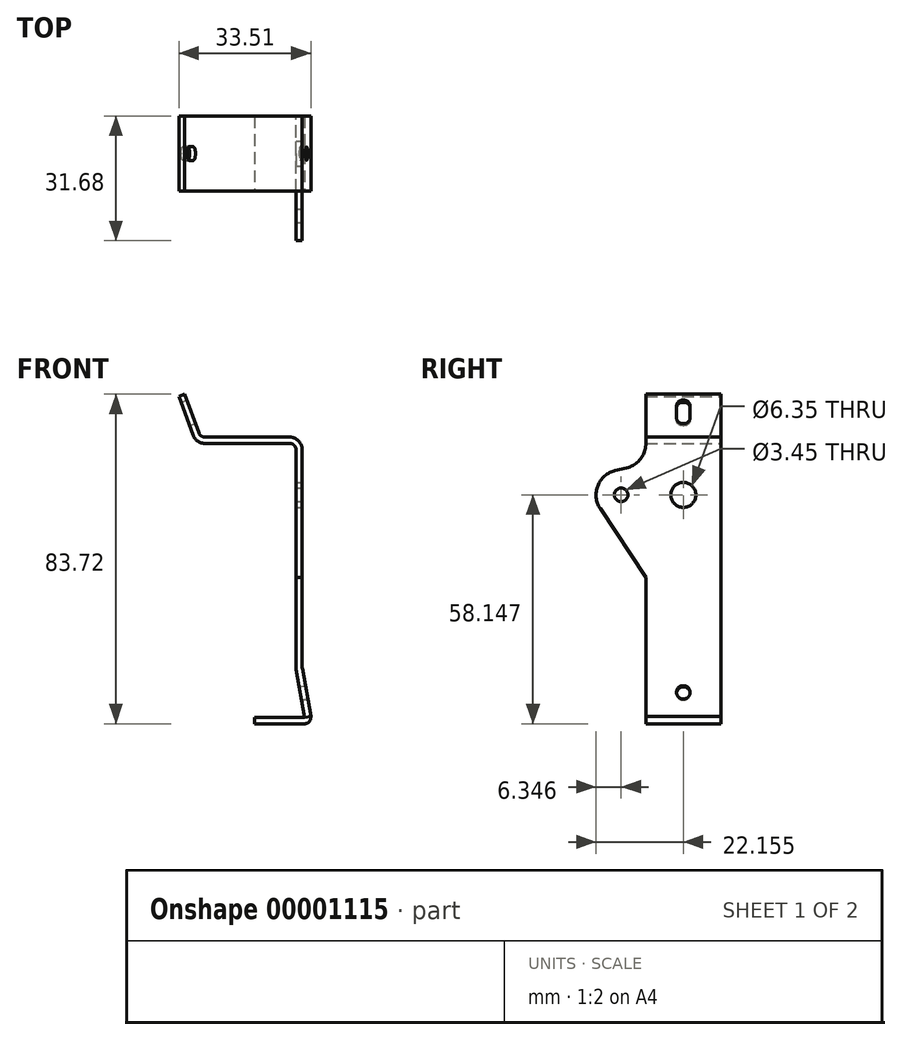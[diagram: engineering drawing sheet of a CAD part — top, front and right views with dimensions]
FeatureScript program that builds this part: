
annotation { "Feature Type Name" : "Feature", "Feature Type Description" : "" }
export const myFeature = defineFeature(function(context is Context, id is Id, definition is map)
    precondition{}
    {
        {
            var Q0;
            Q0=qCreatedBy(makeId("Front.planeOp"),FACE);
            var sketch = newSketch(context, id + "F0", { "sketchPlane" : qUnion([Q0])});
            skLineSegment(sketch, "E0", {"start": v(0, 0.28) * mm, "end": v(0, 55.56) * mm});
            skLineSegment(sketch, "E1", {"start": v(-1.59, 57.15) * mm, "end": v(-23.18, 57.15) * mm});
            skLineSegment(sketch, "E2", {"start": v(-26.16, 59.24) * mm, "end": v(-29.74, 69.08) * mm});
            skLineSegment(sketch, "E3", {"start": v(0.05, -0.27) * mm, "end": v(2.2, -12.5) * mm});
            skLineSegment(sketch, "E4.0", {"start": v(-24.67, 59.78) * mm, "end": v(-28.25, 69.63) * mm});
            skLineSegment(sketch, "E4.1", {"start": v(-1.59, 58.74) * mm, "end": v(-23.18, 58.74) * mm});
            skLineSegment(sketch, "E4.2", {"start": v(1.59, 0.28) * mm, "end": v(1.59, 55.56) * mm});
            skLineSegment(sketch, "E4.3", {"start": v(1.61, 0) * mm, "end": v(3.77, -12.23) * mm});
            skLineSegment(sketch, "E5", {"start": v(-29.74, 69.08) * mm, "end": v(-28.25, 69.63) * mm});
            skLineSegment(sketch, "E6", {"start": v(3.77, -12.23) * mm, "end": v(2.2, -12.5) * mm});
            skPoint(sketch, "E7.visualSharp", {"position": v(1.59, 58.74) * mm});
            skArc(sketch, "E7.filletArc", {"start": v(1.59, 55.56) * mm, "mid": v(0.66, 57.8) * mm, "end": v(-1.59, 58.74) * mm});
            skPoint(sketch, "E8.visualSharp", {"position": v(-25.4, 57.15) * mm});
            skArc(sketch, "E8.filletArc", {"start": v(-26.16, 59.24) * mm, "mid": v(-25, 57.72) * mm, "end": v(-23.18, 57.15) * mm});
            skPoint(sketch, "E9.visualSharp", {"position": v(0, 0) * mm});
            skArc(sketch, "E9.filletArc", {"start": v(0, 0.28) * mm, "mid": v(0.01, 0) * mm, "end": v(0.05, -0.27) * mm});
            skPoint(sketch, "E10.visualSharp", {"position": v(0, 57.15) * mm});
            skArc(sketch, "E10.filletArc", {"start": v(0, 55.56) * mm, "mid": v(-0.46, 56.69) * mm, "end": v(-1.59, 57.15) * mm});
            skPoint(sketch, "E11.visualSharp", {"position": v(-24.29, 58.74) * mm});
            skArc(sketch, "E11.filletArc", {"start": v(-24.67, 59.78) * mm, "mid": v(-24.09, 59.02) * mm, "end": v(-23.18, 58.74) * mm});
            skPoint(sketch, "E12.visualSharp", {"position": v(1.59, 0.14) * mm});
            skArc(sketch, "E12.filletArc", {"start": v(1.59, 0.28) * mm, "mid": v(1.6, 0.14) * mm, "end": v(1.61, 0) * mm});
            skPoint(sketch, "E13", {"position": v(-26.46, 64.7) * mm});
            skPoint(sketch, "E14", {"position": v(-27.95, 64.16) * mm});
            skPoint(sketch, "E15", {"position": v(2.7, -6.11) * mm});
            skPoint(sketch, "E16", {"position": v(1.13, -6.4) * mm});
            skSolve(sketch);
        }
        {
            var Q0;
            Q0=makeQuery(id+"F0.imprint","IMPRINT",FACE,{"disambiguationData":[TD([[makeQuery(id+"F0.imprint","IMPRINT",EDGE,{"derivedFrom":sQuery(id+"F0.wireOp",EDGE,"E0")}),-1.0]])]});
            extrude(context, id + "F1", {"entities" : qUnion([Q0]), "depth" : 19.05 * mm});
        }
        {
            var Q0;
            Q0=makeQuery(id+"F1.opExtrude","SWEPT_FACE",FACE,{"disambiguationData":[OSD([sQuery(id+"F0.wireOp",EDGE,"E4.0")])]});
            var sketch = newSketch(context, id + "F2", { "sketchPlane" : qUnion([Q0])});
            skLineSegment(sketch, "E17.right", {"start": v(0, 75.1) * mm, "end": v(0, 69.85) * mm});
            skLineSegment(sketch, "E18", {"start": v(-11.25, 68.74) * mm, "end": v(-11.25, 71.92) * mm});
            skLineSegment(sketch, "E19", {"start": v(-7.8, 71.92) * mm, "end": v(-7.8, 68.74) * mm});
            skLineSegment(sketch, "E20", {"start": v(-9.66, 73.5) * mm, "end": v(-9.39, 73.5) * mm});
            skLineSegment(sketch, "E21", {"start": v(-9.39, 67.15) * mm, "end": v(-9.66, 67.15) * mm});
            skPoint(sketch, "E22.visualSharp", {"position": v(-11.25, 73.5) * mm});
            skArc(sketch, "E22.filletArc", {"start": v(-9.66, 73.5) * mm, "mid": v(-10.79, 73.04) * mm, "end": v(-11.25, 71.92) * mm});
            skPoint(sketch, "E23.visualSharp", {"position": v(-7.8, 73.5) * mm});
            skArc(sketch, "E23.filletArc", {"start": v(-7.8, 71.92) * mm, "mid": v(-8.26, 73.04) * mm, "end": v(-9.39, 73.5) * mm});
            skPoint(sketch, "E24.visualSharp", {"position": v(-7.8, 67.15) * mm});
            skArc(sketch, "E24.filletArc", {"start": v(-9.39, 67.15) * mm, "mid": v(-8.26, 67.62) * mm, "end": v(-7.8, 68.74) * mm});
            skPoint(sketch, "E25.visualSharp", {"position": v(-11.25, 67.15) * mm});
            skArc(sketch, "E25.filletArc", {"start": v(-11.25, 68.74) * mm, "mid": v(-10.79, 67.62) * mm, "end": v(-9.66, 67.15) * mm});
            skSolve(sketch);
        }
        {
            var Q0;
            Q0=makeQuery(id+"F2.imprint","IMPRINT",FACE,{"disambiguationData":[TD([[makeQuery(id+"F2.imprint","IMPRINT",EDGE,{"derivedFrom":sQuery(id+"F2.wireOp",EDGE,"E18")}),-1.0]])]});
            extrude(context, id + "F3", {"entities" : qUnion([Q0]), "operationType" : NewBodyOperationType.REMOVE, "oppositeDirection" : true, "depth" : 25.4 * mm});
        }
        {
            var Q0;
            Q0=makeQuery(id+"F1.opExtrude","SWEPT_FACE",FACE,{"disambiguationData":[OSD([sQuery(id+"F0.wireOp",EDGE,"E4.3")])]});
            var sketch = newSketch(context, id + "F4", { "sketchPlane" : qUnion([Q0])});
            skCircle(sketch, "E26", {"center": v(-9.53, -6.49) * mm, "radius": 1.73 * mm});
            skSolve(sketch);
        }
        {
            var Q0;
            Q0=makeQuery(id+"F4.imprint","IMPRINT",FACE,{"disambiguationData":[TD([[makeQuery(id+"F4.imprint","IMPRINT",EDGE,{"derivedFrom":sQuery(id+"F4.wireOp",EDGE,"E26")}),1.0]])]});
            extrude(context, id + "F5", {"entities" : qUnion([Q0]), "operationType" : NewBodyOperationType.REMOVE, "oppositeDirection" : true, "depth" : 25.4 * mm});
        }
        {
            var Q0;
            Q0=makeQuery(id+"F1.opExtrude","SWEPT_FACE",FACE,{"disambiguationData":[OSD([sQuery(id+"F0.wireOp",EDGE,"E4.2")])]});
            var sketch = newSketch(context, id + "F6", { "sketchPlane" : qUnion([Q0])});
            skLineSegment(sketch, "E27", {"start": v(-19.05, 55.56) * mm, "end": v(-19.05, 52.1) * mm});
            skLineSegment(sketch, "E28", {"start": v(-19.05, 52.1) * mm, "end": v(-26.82, 50.23) * mm});
            skLineSegment(sketch, "E29", {"start": v(-30.63, 40.55) * mm, "end": v(-19.05, 23.05) * mm});
            skPoint(sketch, "E30.visualSharp", {"position": v(-35.63, 48.11) * mm});
            skArc(sketch, "E30.filletArc", {"start": v(-26.82, 50.23) * mm, "mid": v(-31.24, 46.38) * mm, "end": v(-30.63, 40.55) * mm});
            skPoint(sketch, "E31.0.MirrorP", {"position": v(16.58, 48.11) * mm});
            skArc(sketch, "E31.1.MirrorCS", {"start": v(7.77, 50.23) * mm, "mid": v(12.2, 46.38) * mm, "end": v(11.58, 40.55) * mm});
            skLineSegment(sketch, "E31.2.MirrorCS", {"start": v(11.58, 40.55) * mm, "end": v(0, 23.05) * mm});
            skLineSegment(sketch, "E31.3.MirrorCS", {"start": v(0, 52.1) * mm, "end": v(7.77, 50.23) * mm});
            skSolve(sketch);
        }
        {
            var Q0;
            {var subQ2=sQuery(id+"F6.wireOp",EDGE,"E28");Q0=makeQuery(id+"F6.imprint","IMPRINT",FACE,{"disambiguationData":[TD([[makeQuery(id+"F6.imprint","IMPRINT",EDGE,{"derivedFrom":subQ2}),1.0]])]});}
            var Q1;
            Q1=makeQuery(id+"F6.imprint","IMPRINT",FACE,{"disambiguationData":[TD([[makeQuery(id+"F6.imprint","IMPRINT",EDGE,{"derivedFrom":sQuery(id+"F6.wireOp",EDGE,"E31.1.MirrorCS")}),-1.0]])]});
            extrude(context, id + "F7", {"entities" : qUnion([Q0, Q1]), "operationType" : NewBodyOperationType.ADD, "oppositeDirection" : true, "depth" : 1.59 * mm});
        }
        {
            var Q0;
            {var subQ0=sQuery(id+"F0.wireOp",EDGE,"E4.2");Q0=makeQuery(id+"F7.boolean.opBoolean","MERGE",FACE,{"derivedFrom":[makeQuery(id+"F1.opExtrude","SWEPT_FACE",FACE,{"disambiguationData":[OSD([subQ0])]}),makeQuery(id+"F7.opExtrude","CAP_FACE",FACE,{"disambiguationData":[OSD([subQ0,sQuery(id+"F6.wireOp",EDGE,"E28"),sQuery(id+"F6.wireOp",EDGE,"E29"),sQuery(id+"F6.wireOp",EDGE,"E30.filletArc")])],"isStart":true}),makeQuery(id+"F7.opExtrude","CAP_FACE",FACE,{"disambiguationData":[OSD([subQ0,sQuery(id+"F6.wireOp",EDGE,"E31.1.MirrorCS"),sQuery(id+"F6.wireOp",EDGE,"E31.2.MirrorCS"),sQuery(id+"F6.wireOp",EDGE,"E31.3.MirrorCS")])],"isStart":true})]});}
            var sketch = newSketch(context, id + "F8", { "sketchPlane" : qUnion([Q0])});
            skCircle(sketch, "E32", {"center": v(-25.33, 44.06) * mm, "radius": 1.73 * mm});
            skCircle(sketch, "E33", {"center": v(6.28, 44.06) * mm, "radius": 1.73 * mm});
            skCircle(sketch, "E34", {"center": v(-9.53, 44.06) * mm, "radius": 3.18 * mm});
            skSolve(sketch);
        }
        {
            var Q0;
            {Q0=qUnion([makeQuery(id+"F8.imprint","IMPRINT",FACE,{"disambiguationData":[TD([[makeQuery(id+"F8.imprint","IMPRINT",EDGE,{"derivedFrom":sQuery(id+"F8.wireOp",EDGE,"E32")}),1.0]])]}),makeQuery(id+"F8.imprint","IMPRINT",FACE,{"disambiguationData":[TD([[makeQuery(id+"F8.imprint","IMPRINT",EDGE,{"derivedFrom":sQuery(id+"F8.wireOp",EDGE,"E33")}),1.0]])]}),makeQuery(id+"F8.imprint","IMPRINT",FACE,{"disambiguationData":[TD([[makeQuery(id+"F8.imprint","IMPRINT",EDGE,{"derivedFrom":sQuery(id+"F8.wireOp",EDGE,"E34")}),1.0]])]})]);}
            extrude(context, id + "F9", {"entities" : qUnion([Q0]), "operationType" : NewBodyOperationType.REMOVE, "oppositeDirection" : true, "depth" : 25.4 * mm});
        }
        {
            var Q0;
            Q0=makeQuery(id+"F7.opExtrude","SWEPT_EDGE",EDGE,{"disambiguationData":[OSD([sQuery(id+"F0.wireOp",EDGE,"E4.2"),sQuery(id+"F6.wireOp",EDGE,"E27"),sQuery(id+"F6.wireOp",EDGE,"E28")])]});
            var Q1;
            Q1=makeQuery(id+"F7.opExtrude","SWEPT_EDGE",EDGE,{"disambiguationData":[OSD([sQuery(id+"F0.wireOp",EDGE,"E4.2"),sQuery(id+"F6.wireOp",EDGE,"E31.3.MirrorCS")])]});
            var Q2;
            Q2=makeQuery(id+"F7.opExtrude","SWEPT_EDGE",EDGE,{"disambiguationData":[OSD([sQuery(id+"F0.wireOp",EDGE,"E4.2"),sQuery(id+"F6.wireOp",EDGE,"E31.2.MirrorCS")])]});
            var Q3;
            Q3=makeQuery(id+"F7.opExtrude","SWEPT_EDGE",EDGE,{"disambiguationData":[OSD([sQuery(id+"F0.wireOp",EDGE,"E4.2"),sQuery(id+"F6.wireOp",EDGE,"E29")])]});
            fillet(context, id + "F10", {"entities" : qUnion([Q0, Q1, Q2, Q3]), "radius" : 6.35 * mm, "tangentPropagation" : true, "allowEdgeOverflow" : false});
        }
        {
            var Q0;
            {var subQ0=sQuery(id+"F0.wireOp",EDGE,"E0");var subQ1=sQuery(id+"F0.wireOp",EDGE,"E3");var subQ2=sQuery(id+"F0.wireOp",EDGE,"E4.2");var subQ3=sQuery(id+"F0.wireOp",EDGE,"E4.3");var subQ4=sQuery(id+"F0.wireOp",EDGE,"E6");var subQ5=sQuery(id+"F0.wireOp",EDGE,"E9.filletArc");var subQ6=sQuery(id+"F0.wireOp",EDGE,"E12.filletArc");Q0=makeQuery(id+"F7.boolean.opBoolean","SPLIT",FACE,{"disambiguationData":[TD([makeQuery(id+"F1.opExtrude","SWEPT_FACE",FACE,{"disambiguationData":[OSD([subQ1])]})])],"derivedFrom":makeQuery(id+"F1.opExtrude","CAP_FACE",FACE,{"disambiguationData":[OSD([subQ0,sQuery(id+"F0.wireOp",EDGE,"E1"),sQuery(id+"F0.wireOp",EDGE,"E2"),subQ1,sQuery(id+"F0.wireOp",EDGE,"E4.0"),sQuery(id+"F0.wireOp",EDGE,"E4.1"),subQ2,subQ3,sQuery(id+"F0.wireOp",EDGE,"E5"),subQ4,sQuery(id+"F0.wireOp",EDGE,"E7.filletArc"),sQuery(id+"F0.wireOp",EDGE,"E8.filletArc"),subQ5,sQuery(id+"F0.wireOp",EDGE,"E10.filletArc"),sQuery(id+"F0.wireOp",EDGE,"E11.filletArc"),subQ6])],"isStart":false})});}
            var sketch = newSketch(context, id + "F11", { "sketchPlane" : qUnion([Q0])});
            skLineSegment(sketch, "E35", {"start": v(2.2, -12.5) * mm, "end": v(-10.5, -12.5) * mm});
            skLineSegment(sketch, "E36", {"start": v(-10.5, -12.5) * mm, "end": v(-10.5, -14.1) * mm});
            skLineSegment(sketch, "E37", {"start": v(-10.5, -14.1) * mm, "end": v(3.77, -14.1) * mm});
            skLineSegment(sketch, "E38", {"start": v(3.77, -14.1) * mm, "end": v(3.77, -12.23) * mm});
            skSolve(sketch);
        }
        {
            var Q0;
            Q0=makeQuery(id+"F11.imprint","IMPRINT",FACE,{"disambiguationData":[TD([[makeQuery(id+"F11.imprint","IMPRINT",EDGE,{"derivedFrom":sQuery(id+"F11.wireOp",EDGE,"E35")}),1.0]])]});
            extrude(context, id + "F12", {"entities" : qUnion([Q0]), "oppositeDirection" : true, "depth" : 19.05 * mm});
        }
        {
            var Q0;
            Q0=makeQuery(id+"F12.opExtrude","SWEPT_EDGE",EDGE,{"disambiguationData":[OSD([sQuery(id+"F11.wireOp",EDGE,"E37"),sQuery(id+"F11.wireOp",EDGE,"E38")])]});
            fillet(context, id + "F13", {"entities" : qUnion([Q0]), "radius" : 1.59 * mm, "tangentPropagation" : true, "allowEdgeOverflow" : false});
        }
    });
